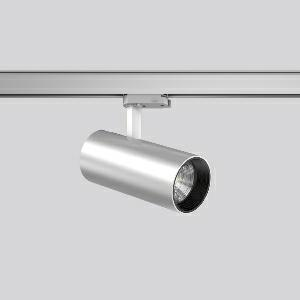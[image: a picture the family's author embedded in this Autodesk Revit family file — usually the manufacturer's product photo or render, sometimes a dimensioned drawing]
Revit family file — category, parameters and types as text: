
# Revit family: deecos_s_mini_742198_004_2_76_9ccb
name_source: partatom
category: Lighting Fixtures
units: mm (PartAtom-declared; Revit-internal decimal feet)

## family parameters
Cut with Voids When Loaded = No
Host = Face
Light Source = No
Part Type = Normal
Room Calculation Point = No
Round Connector Dimension = Use Diameter
Shared = No

## types (1)
- DEECOS S mini (1 x LED Modul 927, 2100 lm, 2700)
    Apparent Load = 20 VA
    Approval mark = CE
    CIE Flux Codes = 99 100 100 100 100
    Color Rendering = 92
    Color Temperature = 2700
    Default Elevation = 1800 mm
    Description = Series: DEECOS S mini
LED surface-mounted projector in modern design with no visible cooling ribs. Housing: die-cast aluminium, powder-coated. Rotation range: 356°. Swivel range: 90°. Black plastic ring and recessed LED to prevent glare from the side. Optical assembly with lens made of plastic (polycarbonate) for the best homogeneous light distribution - can be changed without tools. Best colour rendering index Ra>90. With adapter for RZB 3-circuit DALI tracks. Suitable for Track on ceiling, Wall track. High quality converter without flickering and stroboscopic effect. The following accessories can be mounted without use of tools: interchangeable lenses, decorative glasses, honeycomb louvre, clear and frosted diffusers, white interchangeable plastic ring. 
Colour: silver
Diameter: 87 mm
Height: 214 mm
Lamp: LED
Socket: without socket
Colour temperature: 2700K
Colour rendering index (CRI): 92
System power: 20 W
Rated luminous flux: 2100 lm
Luminous efficiency: 105 lm/W
Control gear: Converter, dimmable, DALI
Protection class: I
Type of protection: IP 20
    Height = 214 mm
    Lamp = 1 x LED Modul 927
    Lamp Light Flux = 2100 lm
    Lamp count = 1
    Length = 87 mm
    Lifetime = 50000 h
    Luminous efficacy = 105 lm/W
    Manufacturer = RZB
    ModVariant = No
    Model = 742198.004.2.76
    Mounting Place = Ceiling
    Mounting Type = Rail mounted
    Number of Poles = 1
    OnlyDefault = Yes
    Power Factor = 1
    Product Name = DEECOS S mini
    Product group = Track mounted projectors
    ProductGroupID = 301
    Protection Class = Protection class I
    Protection Degree = IP 20
    RLX_Detail_Level = 1
    RLX_Emergency_Light_Flux = 0 lm
    RLX_Emergency_Type = 0
    RLX_Emergency_Type_DB = No
    RlxData = <blob elided: 37285 chars, md5=75737a51>
    Socket = socket
    Standby Power = 0 W
    System Light Flux = 2100 lm
    System Power = 20 W
    Type Comments = Product without accessories
    Type Image = 741930.004.jpg
    URL = http://relux.com
    VarID = ---
    Voltage = 230 V
    Voltage Range = 220-240 V
    Weight = 0.00 kg
    Width = 0 mm  [stored 0 ft]

note: [stored X ft] marks values corroborated as IEEE doubles in the binary element streams (Revit-internal decimal feet)

## geometry (parser evidence)
native form markers: Blend x4, Sweep x11
no freeform markers — native parametric forms only
